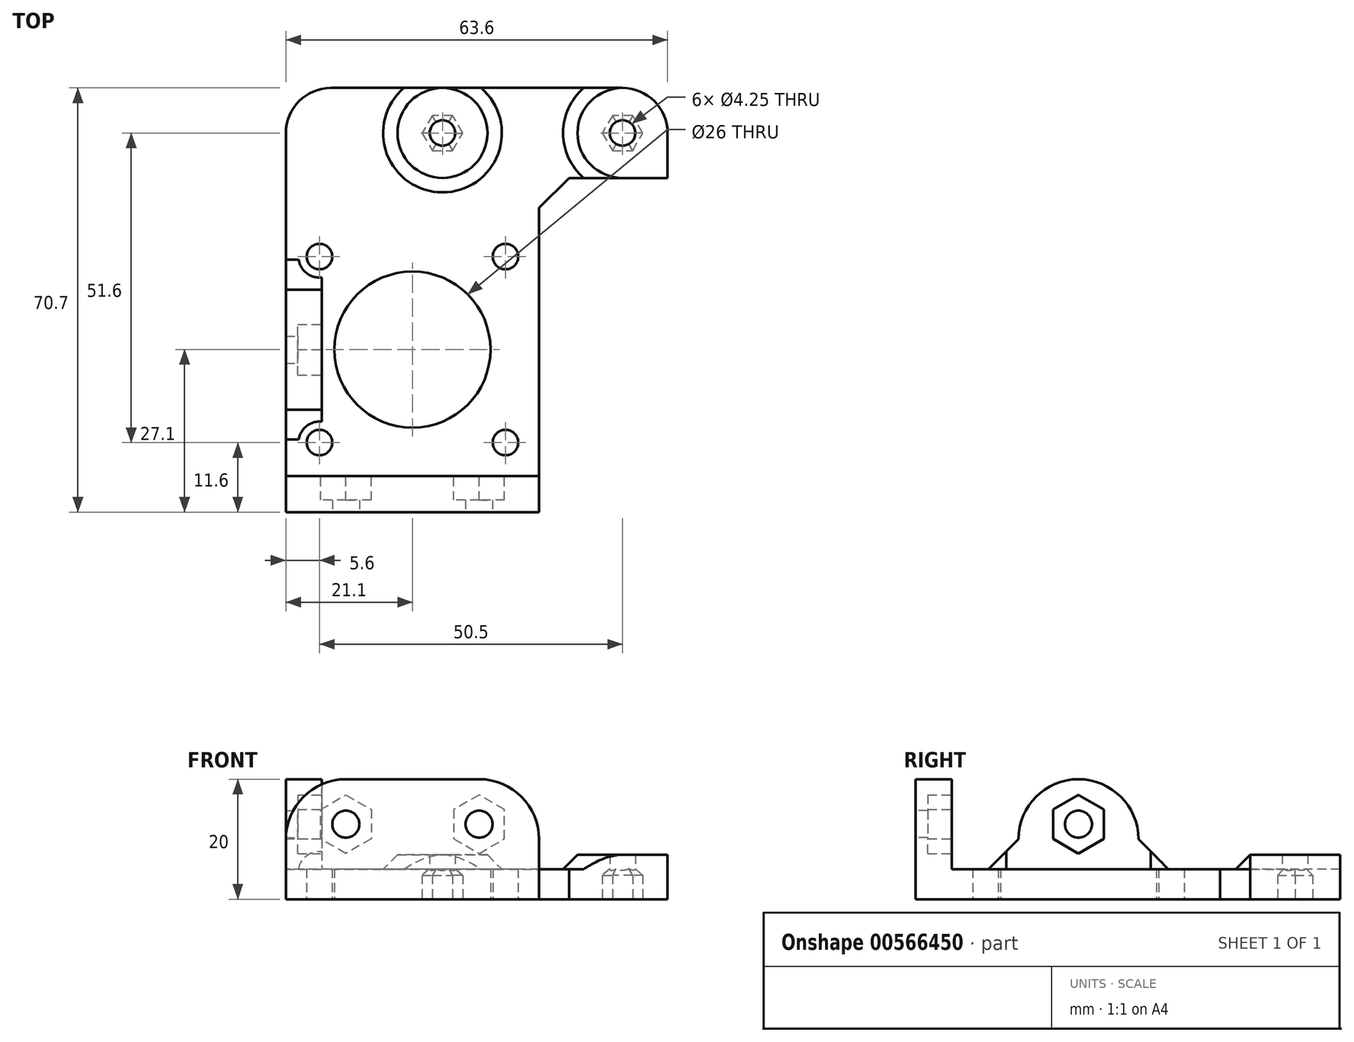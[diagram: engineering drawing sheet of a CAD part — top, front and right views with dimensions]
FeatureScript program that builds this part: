
annotation { "Feature Type Name" : "Feature", "Feature Type Description" : "" }
export const myFeature = defineFeature(function(context is Context, id is Id, definition is map)
    precondition{}
    {
        {
            var Q0;
            Q0=qCreatedBy(makeId("Top.planeOp"),FACE);
            var sketch = newSketch(context, id + "F0", { "sketchPlane" : qUnion([Q0])});
            skCircle(sketch, "E0", {"center": v(0, 0) * mm, "radius": 13 * mm});
            skLineSegment(sketch, "E1.bottom", {"start": v(15.5, -15.5) * mm, "end": v(-15.5, -15.5) * mm, "construction": true});
            skLineSegment(sketch, "E1.top", {"start": v(15.5, 15.5) * mm, "end": v(-15.5, 15.5) * mm, "construction": true});
            skLineSegment(sketch, "E1.left", {"start": v(15.5, -15.5) * mm, "end": v(15.5, 15.5) * mm, "construction": true});
            skLineSegment(sketch, "E1.right", {"start": v(-15.5, -15.5) * mm, "end": v(-15.5, 15.5) * mm, "construction": true});
            skCircle(sketch, "E2", {"center": v(-15.5, 15.5) * mm, "radius": 2.12 * mm});
            skCircle(sketch, "E3", {"center": v(15.5, 15.5) * mm, "radius": 2.12 * mm});
            skCircle(sketch, "E4", {"center": v(15.5, -15.5) * mm, "radius": 2.12 * mm});
            skCircle(sketch, "E5", {"center": v(-15.5, -15.5) * mm, "radius": 2.12 * mm});
            skLineSegment(sketch, "E6.bottom", {"start": v(21.1, -21.1) * mm, "end": v(-21.1, -21.1) * mm});
            skLineSegment(sketch, "E6.top", {"start": v(21.1, 21.1) * mm, "end": v(-21.1, 21.1) * mm, "construction": true});
            skLineSegment(sketch, "E6.left", {"start": v(21.1, -21.1) * mm, "end": v(21.1, 21.1) * mm});
            skLineSegment(sketch, "E6.right", {"start": v(-21.1, -21.1) * mm, "end": v(-21.1, 21.1) * mm});
            skCircle(sketch, "E7", {"center": v(5, 36.1) * mm, "radius": 2.12 * mm});
            skCircle(sketch, "E8", {"center": v(5, 36.1) * mm, "radius": 12.5 * mm, "construction": true});
            skLineSegment(sketch, "E9", {"start": v(5, 36.1) * mm, "end": v(0, 36.1) * mm, "construction": true});
            skLineSegment(sketch, "E10", {"start": v(5, 36.1) * mm, "end": v(5, 21.1) * mm, "construction": true});
            skCircle(sketch, "E11", {"center": v(35, 36.1) * mm, "radius": 2.12 * mm});
            skLineSegment(sketch, "E12", {"start": v(-21.1, 21.1) * mm, "end": v(-21.1, 28.6) * mm});
            skLineSegment(sketch, "E13", {"start": v(21.1, 28.6) * mm, "end": v(21.1, 21.1) * mm});
            skLineSegment(sketch, "E14", {"start": v(0, 43.6) * mm, "end": v(42.5, 43.6) * mm});
            skLineSegment(sketch, "E15", {"start": v(21.1, 28.6) * mm, "end": v(42.5, 28.6) * mm});
            skLineSegment(sketch, "E16", {"start": v(0, 43.6) * mm, "end": v(-21.1, 43.6) * mm});
            skLineSegment(sketch, "E17.MirrorCS", {"start": v(42.5, 43.6) * mm, "end": v(42.5, 28.6) * mm});
            skLineSegment(sketch, "E18", {"start": v(-21.1, 28.6) * mm, "end": v(-21.1, 43.6) * mm});
            skPoint(sketch, "E19.orphan", {"position": v(-42.5, 43.6) * mm});
            skSolve(sketch);
        }
        {
            var Q0;
            Q0=qSketchRegion(id+"F0",true);
            extrude(context, id + "F1", {"entities" : qUnion([Q0]), "depth" : 5 * mm, "offsetDistance" : 25 * mm});
        }
        {
            var Q0;
            Q0=qCreatedBy(makeId("Top.planeOp"),FACE);
            var sketch = newSketch(context, id + "F2", { "sketchPlane" : qUnion([Q0])});
            skLineSegment(sketch, "E20", {"start": v(21.1, -21.1) * mm, "end": v(21.1, -27.1) * mm});
            skLineSegment(sketch, "E21", {"start": v(21.1, -27.1) * mm, "end": v(-21.1, -27.1) * mm});
            skLineSegment(sketch, "E22", {"start": v(-21.1, -10) * mm, "end": v(-21.1, 10) * mm});
            skLineSegment(sketch, "E23", {"start": v(-15.1, 10) * mm, "end": v(-15.1, -10) * mm});
            skLineSegment(sketch, "E24", {"start": v(-15.1, -21.1) * mm, "end": v(21.1, -21.1) * mm});
            skLineSegment(sketch, "E25", {"start": v(-21.1, 10) * mm, "end": v(-15.1, 10) * mm});
            skLineSegment(sketch, "E26.MirrorCS", {"start": v(-21.1, -10) * mm, "end": v(-15.1, -10) * mm});
            skLineSegment(sketch, "E27", {"start": v(-15.1, -21.1) * mm, "end": v(-21.1, -21.1) * mm});
            skLineSegment(sketch, "E28", {"start": v(-21.1, -21.1) * mm, "end": v(-21.1, -27.1) * mm});
            skSolve(sketch);
        }
        {
            var Q0;
            Q0=qSketchRegion(id+"F2",true);
            extrude(context, id + "F3", {"entities" : qUnion([Q0]), "operationType" : NewBodyOperationType.ADD, "depth" : 20 * mm, "offsetDistance" : 25 * mm});
        }
        {
            var Q0;
            Q0=makeQuery(id+"F3.opExtrude","SWEPT_FACE",FACE,{"disambiguationData":[OSD([sQuery(id+"F2.wireOp",EDGE,"E21")])]});
            var sketch = newSketch(context, id + "F4", { "sketchPlane" : qUnion([Q0])});
            skCircle(sketch, "E29", {"center": v(11.1, 12.5) * mm, "radius": 2.25 * mm});
            skCircle(sketch, "E30.MirrorC", {"center": v(-11.1, 12.5) * mm, "radius": 2.25 * mm});
            skSolve(sketch);
        }
        {
            var Q0;
            Q0=qSketchRegion(id+"F4",true);
            extrude(context, id + "F5", {"entities" : qUnion([Q0]), "operationType" : NewBodyOperationType.REMOVE, "oppositeDirection" : true, "depth" : 25 * mm, "offsetDistance" : 25 * mm});
        }
        {
            var Q0;
            Q0=makeQuery(id+"F3.opExtrude","SWEPT_FACE",FACE,{"disambiguationData":[OSD([sQuery(id+"F2.wireOp",EDGE,"E23")])]});
            var sketch = newSketch(context, id + "F6", { "sketchPlane" : qUnion([Q0])});
            skCircle(sketch, "E31", {"center": v(0, 12.5) * mm, "radius": 2.25 * mm});
            skSolve(sketch);
        }
        {
            var Q0;
            Q0=qSketchRegion(id+"F6",true);
            extrude(context, id + "F7", {"entities" : qUnion([Q0]), "operationType" : NewBodyOperationType.REMOVE, "oppositeDirection" : true, "depth" : 25 * mm, "offsetDistance" : 25 * mm});
        }
        {
            var Q0;
            Q0=makeQuery(id+"F3.opExtrude","SWEPT_FACE",FACE,{"disambiguationData":[OSD([sQuery(id+"F2.wireOp",EDGE,"E24"),sQuery(id+"F2.wireOp",EDGE,"E27")])]});
            var sketch = newSketch(context, id + "F8", { "sketchPlane" : qUnion([Q0])});
            skCircle(sketch, "E32.cCircle", {"center": v(-11.1, 12.5) * mm, "radius": 4.22 * mm, "construction": true});
            skLineSegment(sketch, "E32.0", {"start": v(-6.88, 14.94) * mm, "end": v(-6.88, 10.06) * mm});
            skLineSegment(sketch, "E32.1", {"start": v(-6.88, 10.06) * mm, "end": v(-11.1, 7.62) * mm});
            skLineSegment(sketch, "E32.2", {"start": v(-11.1, 7.62) * mm, "end": v(-15.33, 10.06) * mm});
            skLineSegment(sketch, "E32.3", {"start": v(-15.32, 10.06) * mm, "end": v(-15.33, 14.94) * mm});
            skLineSegment(sketch, "E32.4", {"start": v(-15.33, 14.94) * mm, "end": v(-11.1, 17.38) * mm});
            skLineSegment(sketch, "E32.5", {"start": v(-11.1, 17.38) * mm, "end": v(-6.88, 14.94) * mm});
            skPoint(sketch, "E32.0.midPoint", {"position": v(-6.88, 12.5) * mm});
            skLineSegment(sketch, "E33.MirrorCS", {"start": v(11.1, 7.62) * mm, "end": v(15.33, 10.06) * mm});
            skLineSegment(sketch, "E34.MirrorCS", {"start": v(15.32, 10.06) * mm, "end": v(15.33, 14.94) * mm});
            skLineSegment(sketch, "E35.MirrorCS", {"start": v(15.33, 14.94) * mm, "end": v(11.1, 17.38) * mm});
            skLineSegment(sketch, "E36.MirrorCS", {"start": v(11.1, 17.38) * mm, "end": v(6.88, 14.94) * mm});
            skPoint(sketch, "E37.MirrorP", {"position": v(6.88, 12.5) * mm});
            skCircle(sketch, "E38.MirrorC", {"center": v(11.1, 12.5) * mm, "radius": 4.22 * mm, "construction": true});
            skLineSegment(sketch, "E39.MirrorCS", {"start": v(6.88, 10.06) * mm, "end": v(11.1, 7.62) * mm});
            skLineSegment(sketch, "E40.MirrorCS", {"start": v(6.88, 14.94) * mm, "end": v(6.88, 10.06) * mm});
            skSolve(sketch);
        }
        {
            var Q0;
            Q0=qSketchRegion(id+"F8",true);
            extrude(context, id + "F9", {"entities" : qUnion([Q0]), "operationType" : NewBodyOperationType.REMOVE, "oppositeDirection" : true, "depth" : 4 * mm, "offsetDistance" : 25 * mm});
        }
        {
            var Q0;
            Q0=makeQuery(id+"F3.opExtrude","SWEPT_FACE",FACE,{"disambiguationData":[OSD([sQuery(id+"F2.wireOp",EDGE,"E23")])]});
            var sketch = newSketch(context, id + "F10", { "sketchPlane" : qUnion([Q0])});
            skCircle(sketch, "E41.cCircle", {"center": v(0, 12.5) * mm, "radius": 4.22 * mm, "construction": true});
            skLineSegment(sketch, "E41.0", {"start": v(4.22, 14.94) * mm, "end": v(4.22, 10.06) * mm});
            skLineSegment(sketch, "E41.1", {"start": v(4.22, 10.06) * mm, "end": v(0, 7.62) * mm});
            skLineSegment(sketch, "E41.2", {"start": v(0, 7.62) * mm, "end": v(-4.22, 10.06) * mm});
            skLineSegment(sketch, "E41.3", {"start": v(-4.22, 10.06) * mm, "end": v(-4.23, 14.94) * mm});
            skLineSegment(sketch, "E41.4", {"start": v(-4.23, 14.94) * mm, "end": v(0, 17.38) * mm});
            skLineSegment(sketch, "E41.5", {"start": v(0, 17.38) * mm, "end": v(4.22, 14.94) * mm});
            skPoint(sketch, "E41.0.midPoint", {"position": v(4.22, 12.5) * mm});
            skSolve(sketch);
        }
        {
            var Q0;
            Q0=qSketchRegion(id+"F10",true);
            extrude(context, id + "F11", {"entities" : qUnion([Q0]), "operationType" : NewBodyOperationType.REMOVE, "oppositeDirection" : true, "depth" : 4 * mm, "offsetDistance" : 25 * mm});
        }
        {
            var Q0;
            Q0=makeQuery(id+"F1.opExtrude","CAP_EDGE",EDGE,{"disambiguationData":[OSD([sQuery(id+"F0.wireOp",EDGE,"E6.bottom")])],"isStart":false});
            var Q1;
            Q1=makeQuery(id+"F3.boolean.opBoolean","INTERSECT",EDGE,{"derivedFrom":[makeQuery(id+"F1.opExtrude","CAP_FACE",FACE,{"disambiguationData":[OSD([sQuery(id+"F0.wireOp",EDGE,"E0"),sQuery(id+"F0.wireOp",EDGE,"E2"),sQuery(id+"F0.wireOp",EDGE,"E3"),sQuery(id+"F0.wireOp",EDGE,"E4"),sQuery(id+"F0.wireOp",EDGE,"E5"),sQuery(id+"F0.wireOp",EDGE,"E6.bottom"),sQuery(id+"F0.wireOp",EDGE,"E6.top"),sQuery(id+"F0.wireOp",EDGE,"E6.left"),sQuery(id+"F0.wireOp",EDGE,"E6.right")])],"isStart":false}),makeQuery(id+"F3.opExtrude","SWEPT_FACE",FACE,{"disambiguationData":[OSD([sQuery(id+"F2.wireOp",EDGE,"E26.MirrorCS")])]})]});
            var Q2;
            Q2=makeQuery(id+"F3.boolean.opBoolean","INTERSECT",EDGE,{"derivedFrom":[makeQuery(id+"F1.opExtrude","CAP_FACE",FACE,{"disambiguationData":[OSD([sQuery(id+"F0.wireOp",EDGE,"E0"),sQuery(id+"F0.wireOp",EDGE,"E2"),sQuery(id+"F0.wireOp",EDGE,"E3"),sQuery(id+"F0.wireOp",EDGE,"E4"),sQuery(id+"F0.wireOp",EDGE,"E5"),sQuery(id+"F0.wireOp",EDGE,"E6.bottom"),sQuery(id+"F0.wireOp",EDGE,"E6.top"),sQuery(id+"F0.wireOp",EDGE,"E6.left"),sQuery(id+"F0.wireOp",EDGE,"E6.right")])],"isStart":false}),makeQuery(id+"F3.opExtrude","SWEPT_FACE",FACE,{"disambiguationData":[OSD([sQuery(id+"F2.wireOp",EDGE,"E25")])]})]});
            chamfer(context, id + "F12", {"entities" : qUnion([Q0, Q1, Q2]), "width" : 5 * mm, "tangentPropagation" : true});
        }
        {
            var Q0;
            Q0=makeQuery(id+"F12.opChamfer","SPLIT",FACE,{"disambiguationData":[OD(1.0)],"derivedFrom":makeQuery(id+"F1.opExtrude","CAP_FACE",FACE,{"disambiguationData":[OSD([sQuery(id+"F0.wireOp",EDGE,"E0"),sQuery(id+"F0.wireOp",EDGE,"E2"),sQuery(id+"F0.wireOp",EDGE,"E3"),sQuery(id+"F0.wireOp",EDGE,"E4"),sQuery(id+"F0.wireOp",EDGE,"E5"),sQuery(id+"F0.wireOp",EDGE,"E6.bottom"),sQuery(id+"F0.wireOp",EDGE,"E6.top"),sQuery(id+"F0.wireOp",EDGE,"E6.left"),sQuery(id+"F0.wireOp",EDGE,"E6.right")])],"isStart":false})});
            var sketch = newSketch(context, id + "F13", { "sketchPlane" : qUnion([Q0])});
            skCircle(sketch, "E42", {"center": v(-15.5, 15.5) * mm, "radius": 3.5 * mm});
            skCircle(sketch, "E43.MirrorC", {"center": v(-15.5, -15.5) * mm, "radius": 3.5 * mm});
            skCircle(sketch, "E44.MirrorC", {"center": v(15.5, -15.5) * mm, "radius": 3.5 * mm});
            skSolve(sketch);
        }
        {
            var Q0;
            Q0=qSketchRegion(id+"F13",true);
            extrude(context, id + "F14", {"entities" : qUnion([Q0]), "operationType" : NewBodyOperationType.REMOVE, "depth" : 25 * mm, "offsetDistance" : 25 * mm});
        }
        {
            var Q0;
            Q0=makeQuery(id+"F3.opExtrude","CAP_EDGE",EDGE,{"disambiguationData":[OSD([sQuery(id+"F2.wireOp",EDGE,"E26.MirrorCS")])],"isStart":false});
            var Q1;
            Q1=makeQuery(id+"F3.opExtrude","CAP_EDGE",EDGE,{"disambiguationData":[OSD([sQuery(id+"F2.wireOp",EDGE,"E25")])],"isStart":false});
            var Q2;
            Q2=makeQuery(id+"F3.opExtrude","CAP_EDGE",EDGE,{"disambiguationData":[OSD([sQuery(id+"F2.wireOp",EDGE,"E20")])],"isStart":false});
            var Q3;
            Q3=makeQuery(id+"F3.opExtrude","CAP_EDGE",EDGE,{"disambiguationData":[OSD([sQuery(id+"F2.wireOp",EDGE,"E28")])],"isStart":false});
            fillet(context, id + "F15", {"entities" : qUnion([Q0, Q1, Q2, Q3]), "radius" : 10 * mm, "tangentPropagation" : true, "allowEdgeOverflow" : false});
        }
        {
            var Q0;
            Q0=makeQuery(id+"F1.opExtrude","SWEPT_EDGE",EDGE,{"disambiguationData":[OSD([sQuery(id+"F0.wireOp",EDGE,"T0GHFEy0-NdDx-5ELO-U6rn-3qloD0EzuKSv"),sQuery(id+"F0.wireOp",EDGE,"E13")])]});
            chamfer(context, id + "F16", {"entities" : qUnion([Q0]), "width" : 5 * mm, "tangentPropagation" : true});
        }
        {
            var Q0;
            {var subQ0=makeQuery(id+"F1.opExtrude","CAP_FACE",FACE,{"disambiguationData":[OSD([sQuery(id+"F0.wireOp",EDGE,"E0"),sQuery(id+"F0.wireOp",EDGE,"E2"),sQuery(id+"F0.wireOp",EDGE,"E3"),sQuery(id+"F0.wireOp",EDGE,"E4"),sQuery(id+"F0.wireOp",EDGE,"E5"),sQuery(id+"F0.wireOp",EDGE,"E6.bottom"),sQuery(id+"F0.wireOp",EDGE,"E6.left"),sQuery(id+"F0.wireOp",EDGE,"E6.right"),sQuery(id+"F0.wireOp",EDGE,"E7"),sQuery(id+"F0.wireOp",EDGE,"E11"),sQuery(id+"F0.wireOp",EDGE,"51efa23a-cee4-496f-a7cd-2f6e27babf4e0.MirrorC"),sQuery(id+"F0.wireOp",EDGE,"E12"),sQuery(id+"F0.wireOp",EDGE,"E13"),sQuery(id+"F0.wireOp",EDGE,"E14"),sQuery(id+"F0.wireOp",EDGE,"2d6b1f7b-ebd0-46e1-8615-815c405c7aae.trimOffspring"),sQuery(id+"F0.wireOp",EDGE,"RWEpfeJI-ypTu-Pn30-H6ze-dGeE97qbp2gg"),sQuery(id+"F0.wireOp",EDGE,"E15")])],"isStart":false});Q0=makeQuery(id+"F14.boolean.opBoolean","MERGE",FACE,{"derivedFrom":[makeQuery(id+"F12.opChamfer","SPLIT",FACE,{"disambiguationData":[OD(0.0)],"derivedFrom":subQ0}),makeQuery(id+"F12.opChamfer","SPLIT",FACE,{"disambiguationData":[OD(1.0)],"derivedFrom":subQ0}),makeQuery(id+"F14.opExtrude","CAP_FACE",FACE,{"disambiguationData":[OSD([sQuery(id+"F13.wireOp",EDGE,"E42")])],"isStart":true}),makeQuery(id+"F14.opExtrude","CAP_FACE",FACE,{"disambiguationData":[OSD([sQuery(id+"F13.wireOp",EDGE,"E43.MirrorC")])],"isStart":true}),makeQuery(id+"F14.opExtrude","CAP_FACE",FACE,{"disambiguationData":[OSD([sQuery(id+"F13.wireOp",EDGE,"E44.MirrorC")])],"isStart":true})]});}
            var sketch = newSketch(context, id + "F17", { "sketchPlane" : qUnion([Q0])});
            skCircle(sketch, "E45", {"center": v(5, 36.1) * mm, "radius": 7.5 * mm});
            skArc(sketch, "E46", {"start": v(42.5, 36.1) * mm, "mid": v(29.7, 41.4) * mm, "end": v(35, 28.6) * mm});
            skCircle(sketch, "E47", {"center": v(5, 36.1) * mm, "radius": 2.12 * mm});
            skCircle(sketch, "E48", {"center": v(35, 36.1) * mm, "radius": 2.12 * mm});
            skLineSegment(sketch, "E49", {"start": v(42.5, 36.1) * mm, "end": v(42.5, 28.6) * mm});
            skLineSegment(sketch, "E50", {"start": v(42.5, 28.6) * mm, "end": v(35, 28.6) * mm});
            skSolve(sketch);
        }
        {
            var Q0;
            Q0=qSketchRegion(id+"F17",true);
            extrude(context, id + "F18", {"entities" : qUnion([Q0]), "operationType" : NewBodyOperationType.ADD, "depth" : 2.4 * mm, "offsetDistance" : 25 * mm});
        }
        {
            var Q0;
            Q0=makeQuery(id+"F18.opExtrude","CAP_EDGE",EDGE,{"disambiguationData":[OSD([sQuery(id+"F17.wireOp",EDGE,"13gUoJV9-0pN4-28iU-9vl6-GBu1GgRhRDP2")])],"isStart":true});
            var Q1;
            Q1=makeQuery(id+"F18.opExtrude","CAP_EDGE",EDGE,{"disambiguationData":[OSD([sQuery(id+"F17.wireOp",EDGE,"E45")])],"isStart":true});
            var Q2;
            Q2=makeQuery(id+"F18.opExtrude","CAP_EDGE",EDGE,{"disambiguationData":[OSD([sQuery(id+"F17.wireOp",EDGE,"E46")])],"isStart":true});
            chamfer(context, id + "F19", {"entities" : qUnion([Q0, Q1, Q2]), "width" : 2.4 * mm, "tangentPropagation" : true});
        }
        {
            var Q0;
            Q0=makeQuery(id+"F3.boolean.opBoolean","MERGE",FACE,{"derivedFrom":[makeQuery(id+"F1.opExtrude","CAP_FACE",FACE,{"disambiguationData":[OSD([sQuery(id+"F0.wireOp",EDGE,"E0"),sQuery(id+"F0.wireOp",EDGE,"E2"),sQuery(id+"F0.wireOp",EDGE,"E3"),sQuery(id+"F0.wireOp",EDGE,"E4"),sQuery(id+"F0.wireOp",EDGE,"E5"),sQuery(id+"F0.wireOp",EDGE,"E6.bottom"),sQuery(id+"F0.wireOp",EDGE,"E6.left"),sQuery(id+"F0.wireOp",EDGE,"E6.right"),sQuery(id+"F0.wireOp",EDGE,"E7"),sQuery(id+"F0.wireOp",EDGE,"E11"),sQuery(id+"F0.wireOp",EDGE,"51efa23a-cee4-496f-a7cd-2f6e27babf4e0.MirrorC"),sQuery(id+"F0.wireOp",EDGE,"E12"),sQuery(id+"F0.wireOp",EDGE,"E13"),sQuery(id+"F0.wireOp",EDGE,"E14"),sQuery(id+"F0.wireOp",EDGE,"2d6b1f7b-ebd0-46e1-8615-815c405c7aae.trimOffspring"),sQuery(id+"F0.wireOp",EDGE,"RWEpfeJI-ypTu-Pn30-H6ze-dGeE97qbp2gg"),sQuery(id+"F0.wireOp",EDGE,"E15")])],"isStart":true}),makeQuery(id+"F3.opExtrude","CAP_FACE",FACE,{"disambiguationData":[OSD([sQuery(id+"F2.wireOp",EDGE,"E20"),sQuery(id+"F2.wireOp",EDGE,"E21"),sQuery(id+"F2.wireOp",EDGE,"E24"),sQuery(id+"F2.wireOp",EDGE,"E27"),sQuery(id+"F2.wireOp",EDGE,"E28")])],"isStart":true})]});
            var sketch = newSketch(context, id + "F20", { "sketchPlane" : qUnion([Q0])});
            skCircle(sketch, "E51.cCircle", {"center": v(5, -36.1) * mm, "radius": 2.92 * mm, "construction": true});
            skLineSegment(sketch, "E51.0", {"start": v(3.31, -33.18) * mm, "end": v(6.69, -33.18) * mm});
            skLineSegment(sketch, "E51.1", {"start": v(6.69, -33.18) * mm, "end": v(8.37, -36.1) * mm});
            skLineSegment(sketch, "E51.2", {"start": v(8.37, -36.1) * mm, "end": v(6.69, -39.02) * mm});
            skLineSegment(sketch, "E51.3", {"start": v(6.69, -39.02) * mm, "end": v(3.31, -39.02) * mm});
            skLineSegment(sketch, "E51.4", {"start": v(3.31, -39.02) * mm, "end": v(1.63, -36.1) * mm});
            skLineSegment(sketch, "E51.5", {"start": v(1.63, -36.1) * mm, "end": v(3.31, -33.18) * mm});
            skPoint(sketch, "E51.0.midPoint", {"position": v(5, -33.18) * mm});
            skCircle(sketch, "E52.cCircle", {"center": v(35, -36.1) * mm, "radius": 2.92 * mm, "construction": true});
            skLineSegment(sketch, "E52.0", {"start": v(36.69, -39.02) * mm, "end": v(33.31, -39.02) * mm});
            skLineSegment(sketch, "E52.1", {"start": v(33.31, -39.02) * mm, "end": v(31.63, -36.1) * mm});
            skLineSegment(sketch, "E52.2", {"start": v(31.63, -36.1) * mm, "end": v(33.31, -33.18) * mm});
            skLineSegment(sketch, "E52.3", {"start": v(33.31, -33.18) * mm, "end": v(36.69, -33.18) * mm});
            skLineSegment(sketch, "E52.4", {"start": v(36.69, -33.18) * mm, "end": v(38.37, -36.1) * mm});
            skLineSegment(sketch, "E52.5", {"start": v(38.37, -36.1) * mm, "end": v(36.69, -39.02) * mm});
            skPoint(sketch, "E52.0.midPoint", {"position": v(35, -39.02) * mm});
            skSolve(sketch);
        }
        {
            var Q0;
            Q0=qSketchRegion(id+"F20",true);
            extrude(context, id + "F21", {"entities" : qUnion([Q0]), "operationType" : NewBodyOperationType.REMOVE, "oppositeDirection" : true, "depth" : 6 * mm, "offsetDistance" : 25 * mm});
        }
        {
            var Q0;
            Q0=makeQuery(id+"F21.boolean.opBoolean","COPY",EDGE,{"derivedFrom":makeQuery(id+"F21.opExtrude","CAP_EDGE",EDGE,{"disambiguationData":[OSD([sQuery(id+"F20.wireOp",EDGE,"E51.4")])],"isStart":false})});
            var Q1;
            Q1=makeQuery(id+"F21.boolean.opBoolean","COPY",EDGE,{"derivedFrom":makeQuery(id+"F21.opExtrude","CAP_EDGE",EDGE,{"disambiguationData":[OSD([sQuery(id+"F20.wireOp",EDGE,"E51.3")])],"isStart":false})});
            var Q2;
            Q2=makeQuery(id+"F21.boolean.opBoolean","COPY",EDGE,{"derivedFrom":makeQuery(id+"F21.opExtrude","CAP_EDGE",EDGE,{"disambiguationData":[OSD([sQuery(id+"F20.wireOp",EDGE,"E51.2")])],"isStart":false})});
            var Q3;
            Q3=makeQuery(id+"F21.boolean.opBoolean","COPY",EDGE,{"derivedFrom":makeQuery(id+"F21.opExtrude","CAP_EDGE",EDGE,{"disambiguationData":[OSD([sQuery(id+"F20.wireOp",EDGE,"E51.1")])],"isStart":false})});
            var Q4;
            Q4=makeQuery(id+"F21.boolean.opBoolean","COPY",EDGE,{"derivedFrom":makeQuery(id+"F21.opExtrude","CAP_EDGE",EDGE,{"disambiguationData":[OSD([sQuery(id+"F20.wireOp",EDGE,"E51.0")])],"isStart":false})});
            var Q5;
            Q5=makeQuery(id+"F21.boolean.opBoolean","COPY",EDGE,{"derivedFrom":makeQuery(id+"F21.opExtrude","CAP_EDGE",EDGE,{"disambiguationData":[OSD([sQuery(id+"F20.wireOp",EDGE,"E51.5")])],"isStart":false})});
            var Q6;
            Q6=makeQuery(id+"F21.boolean.opBoolean","COPY",EDGE,{"derivedFrom":makeQuery(id+"F21.opExtrude","CAP_EDGE",EDGE,{"disambiguationData":[OSD([sQuery(id+"F20.wireOp",EDGE,"E52.2")])],"isStart":false})});
            var Q7;
            Q7=makeQuery(id+"F21.boolean.opBoolean","COPY",EDGE,{"derivedFrom":makeQuery(id+"F21.opExtrude","CAP_EDGE",EDGE,{"disambiguationData":[OSD([sQuery(id+"F20.wireOp",EDGE,"E52.1")])],"isStart":false})});
            var Q8;
            Q8=makeQuery(id+"F21.boolean.opBoolean","COPY",EDGE,{"derivedFrom":makeQuery(id+"F21.opExtrude","CAP_EDGE",EDGE,{"disambiguationData":[OSD([sQuery(id+"F20.wireOp",EDGE,"E52.3")])],"isStart":false})});
            var Q9;
            Q9=makeQuery(id+"F21.boolean.opBoolean","COPY",EDGE,{"derivedFrom":makeQuery(id+"F21.opExtrude","CAP_EDGE",EDGE,{"disambiguationData":[OSD([sQuery(id+"F20.wireOp",EDGE,"E52.4")])],"isStart":false})});
            var Q10;
            Q10=makeQuery(id+"F21.boolean.opBoolean","COPY",EDGE,{"derivedFrom":makeQuery(id+"F21.opExtrude","CAP_EDGE",EDGE,{"disambiguationData":[OSD([sQuery(id+"F20.wireOp",EDGE,"E52.5")])],"isStart":false})});
            var Q11;
            Q11=makeQuery(id+"F21.boolean.opBoolean","COPY",EDGE,{"derivedFrom":makeQuery(id+"F21.opExtrude","CAP_EDGE",EDGE,{"disambiguationData":[OSD([sQuery(id+"F20.wireOp",EDGE,"E52.0")])],"isStart":false})});
            var Q12;
            Q12=makeQuery(id+"F21.boolean.opBoolean","COPY",EDGE,{"derivedFrom":makeQuery(id+"F21.opExtrude","CAP_EDGE",EDGE,{"disambiguationData":[OSD([sQuery(id+"F20.wireOp",EDGE,"a9bd5471-467a-465d-a3ea-4c4c8a0ff4ae.0")])],"isStart":false})});
            var Q13;
            Q13=makeQuery(id+"F21.boolean.opBoolean","COPY",EDGE,{"derivedFrom":makeQuery(id+"F21.opExtrude","CAP_EDGE",EDGE,{"disambiguationData":[OSD([sQuery(id+"F20.wireOp",EDGE,"a9bd5471-467a-465d-a3ea-4c4c8a0ff4ae.5")])],"isStart":false})});
            var Q14;
            Q14=makeQuery(id+"F21.boolean.opBoolean","COPY",EDGE,{"derivedFrom":makeQuery(id+"F21.opExtrude","CAP_EDGE",EDGE,{"disambiguationData":[OSD([sQuery(id+"F20.wireOp",EDGE,"a9bd5471-467a-465d-a3ea-4c4c8a0ff4ae.1")])],"isStart":false})});
            var Q15;
            Q15=makeQuery(id+"F21.boolean.opBoolean","COPY",EDGE,{"derivedFrom":makeQuery(id+"F21.opExtrude","CAP_EDGE",EDGE,{"disambiguationData":[OSD([sQuery(id+"F20.wireOp",EDGE,"a9bd5471-467a-465d-a3ea-4c4c8a0ff4ae.4")])],"isStart":false})});
            var Q16;
            Q16=makeQuery(id+"F21.boolean.opBoolean","COPY",EDGE,{"derivedFrom":makeQuery(id+"F21.opExtrude","CAP_EDGE",EDGE,{"disambiguationData":[OSD([sQuery(id+"F20.wireOp",EDGE,"a9bd5471-467a-465d-a3ea-4c4c8a0ff4ae.3")])],"isStart":false})});
            var Q17;
            Q17=makeQuery(id+"F21.boolean.opBoolean","COPY",EDGE,{"derivedFrom":makeQuery(id+"F21.opExtrude","CAP_EDGE",EDGE,{"disambiguationData":[OSD([sQuery(id+"F20.wireOp",EDGE,"a9bd5471-467a-465d-a3ea-4c4c8a0ff4ae.2")])],"isStart":false})});
            chamfer(context, id + "F22", {"entities" : qUnion([Q0, Q1, Q2, Q3, Q4, Q5, Q6, Q7, Q8, Q9, Q10, Q11, Q12, Q13, Q14, Q15, Q16, Q17]), "width" : 2 * mm, "tangentPropagation" : true});
        }
        {
            var Q0;
            Q0=makeQuery(id+"F1.opExtrude","SWEPT_EDGE",EDGE,{"disambiguationData":[OSD([sQuery(id+"F0.wireOp",EDGE,"E16"),sQuery(id+"F0.wireOp",EDGE,"TIKiEf2I-xfC2-kMxM-m0qf-Dn47fSwsOD3X")])]});
            var Q1;
            Q1=makeQuery(id+"F1.opExtrude","SWEPT_EDGE",EDGE,{"disambiguationData":[OSD([sQuery(id+"F0.wireOp",EDGE,"E14"),sQuery(id+"F0.wireOp",EDGE,"E17.MirrorCS")])]});
            fillet(context, id + "F23", {"entities" : qUnion([Q0, Q1]), "radius" : 7.5 * mm, "tangentPropagation" : true, "allowEdgeOverflow" : false});
        }
    });
